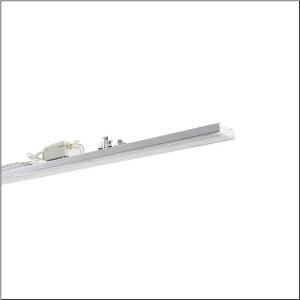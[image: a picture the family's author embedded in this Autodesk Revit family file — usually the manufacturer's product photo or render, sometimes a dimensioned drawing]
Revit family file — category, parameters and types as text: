
# Revit family: licross_11_recessed_mo_51tl18dv6e5g
name_source: partatom
category: Lighting Fixtures
units: mm (PartAtom-declared; Revit-internal decimal feet)

## family parameters
Cut with Voids When Loaded = No
Host = Face
Light Source = No
Part Type = Normal
Room Calculation Point = No
Round Connector Dimension = Use Diameter
Shared = No

## types (1)
- --- (1 x LED, 14560 lm, 84.1 W, 6500K)
    Apparent Load = 84 VA
    CIE Flux Codes = 83 96 99 100 100
    Color Rendering = 80
    Color Temperature = 6500K
    Default Elevation = 1800 mm
    Description = Licross 11 Recessed MO, luminaire insert, of sheet steel, coil coated, white, length: 2.250mm, width: 66mm, height: 67mm, LED rated luminous flux: 14.560lm, light colour: 865, SDCM (Standard Deviation of Colour Matching)MacAdam ≤ 2 SDCM (initial), control gear: DALI 2, with plug, 5-pole, with phase selection, mains connection: 220..240V, AC, 50/60Hz, rated input power: 84W, internal wiring halogen-free, primary light control with lens, of plastic, primary optical cover: cover, of PMMA, light emission: direct distribution, primary light characteristic: symmetric, protection rating (complete): IP40, insulation class (complete): insulation class I (protective earthing), certification: CE, ENEC, VDE, UKCA, protection symbol: D if used in an environment without relevant dust loads with corresponding accessories, impact resistance: IK06, permissible ambient temperature for indoor applications: -25..+35°C, corresponds to IFS (International Featured Standards) requirements for safety and quality in the food industry, reducing of maximum allowable ambient temperature of 5°C with ceiling mounting, LABS conformity tested according to VDMA 24364:2018-05, The light source and the operating device comply with the requirements of the Ecodesign Regulation (EU) 2019/2020 and are replaceable in accordance with this regulation, packaging unit: 1 piece
    Height = 58 mm
    Lamp = 1 x LED
    Lamp Light Flux = 14560 lm
    Lamp Power = 84.1 W
    Lamp count = 1
    Length = 2250 mm
    Luminous efficacy = 173 lm/W
    Manufacturer = Siteco
    ModVariant = No
    Model = 51TL18DV6E5G
    Mounting Place = Ceiling
    Mounting Type = Pendant
    Number of Poles = 1
    OnlyDefault = Yes
    Power Factor = 1
    Product Name = Licross 11 Recessed MO
    Product group = luminaire insert | ceiling pendant
    ProductGroupID = 901
    Protection Class = Protection class I
    Protection Degree = IP 40
    RLX_Detail_Level = 1
    RLX_Emergency_Light_Flux = 0 lm
    RLX_Emergency_Type = 0
    RLX_Emergency_Type_DB = No
    RlxData = <blob elided: 29461 chars, md5=1315c749>
    Socket = socket
    Standby Power = 0 W
    System Light Flux = 14560 lm
    System Power = 84 W
    Type Comments = factory setting: luminous flux: 100 % | dim-lin: 254 | 378 mA
    Type Image = l_1296930.jpg
    URL = http://relux.com
    VarID = @adj_038951
    Voltage = 0 V
    Weight = 0.00 kg
    Width = 66 mm

## geometry (parser evidence)
native form markers: Blend x4, Sweep x9
no freeform markers — native parametric forms only
